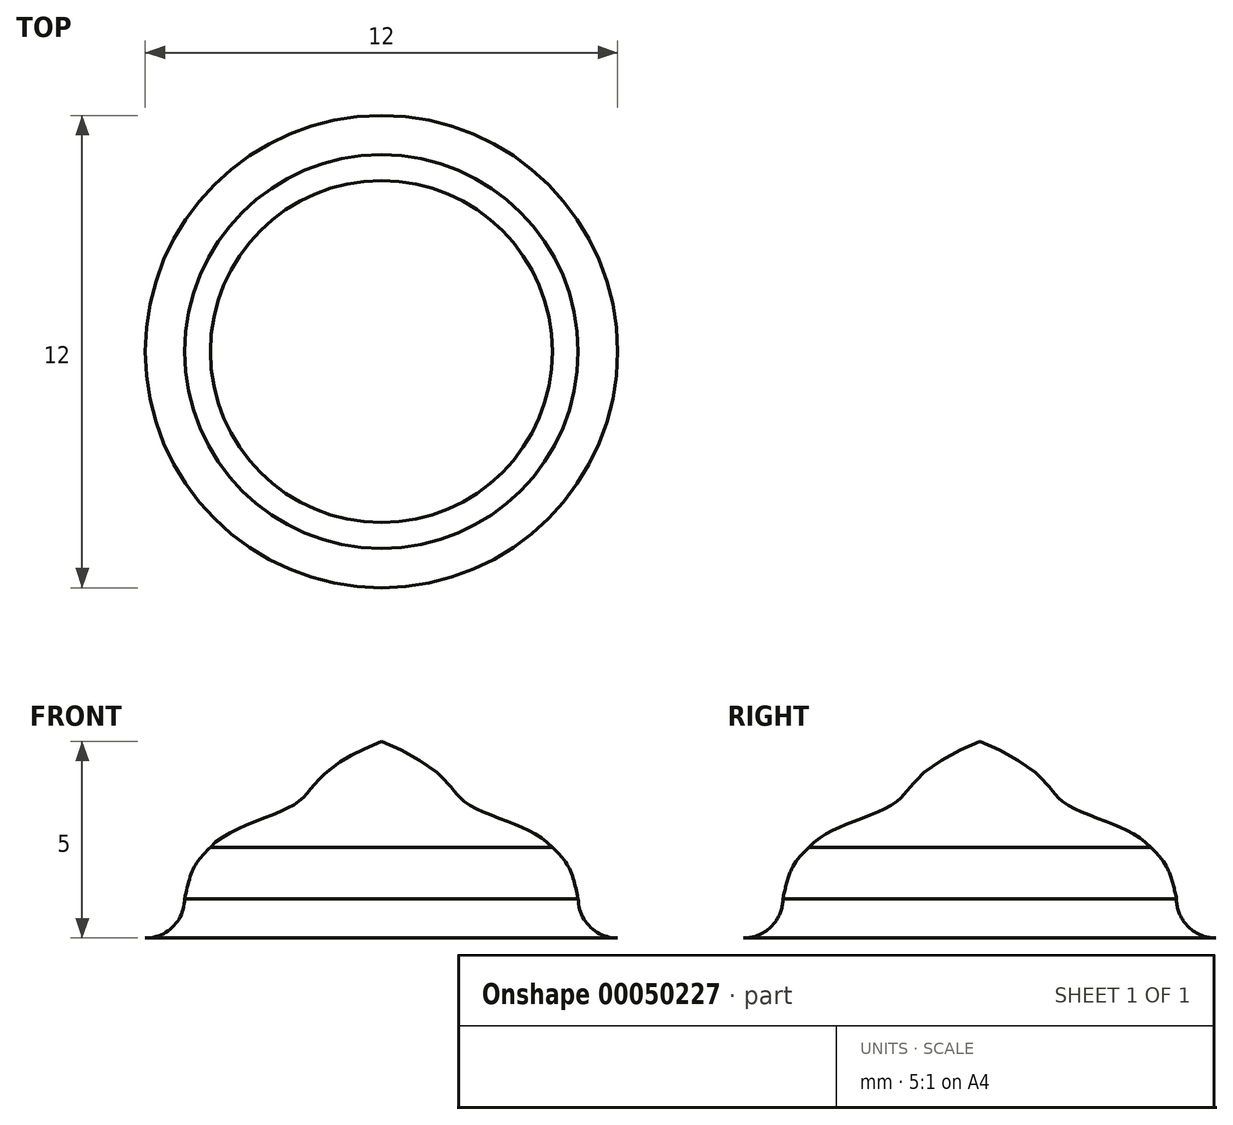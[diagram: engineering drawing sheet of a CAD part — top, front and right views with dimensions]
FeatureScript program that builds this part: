
annotation { "Feature Type Name" : "Feature", "Feature Type Description" : "" }
export const myFeature = defineFeature(function(context is Context, id is Id, definition is map)
    precondition{}
    {
        {
            var Q0;
            Q0=qCreatedBy(makeId("Front.planeOp"),FACE);
            var sketch = newSketch(context, id + "F0", { "sketchPlane" : qUnion([Q0])});
            skLineSegment(sketch, "E0", {"start": v(0, 0) * mm, "end": v(-5, 0) * mm});
            skLineSegment(sketch, "E1", {"start": v(0, -5) * mm, "end": v(0, 0) * mm});
            skFitSpline(sketch, "E2", {"points": [v(-5, 0) * mm, v(-4.34, -2.3) * mm, v(-2.2, -3.4) * mm, v(0, -5) * mm], "startDerivative": vector(4.28, -8.62) * mm, "endDerivative": vector(15.84, -6.66) * mm});
            skLineSegment(sketch, "E3", {"start": v(-5, 0) * mm, "end": v(-6, 0) * mm});
            skLineSegment(sketch, "E4", {"start": v(-5, 0) * mm, "end": v(-5, -1) * mm, "construction": true});
            skArc(sketch, "E5", {"start": v(-5, -1) * mm, "mid": v(-5.3, -0.3) * mm, "end": v(-6, 0) * mm});
            skFitSpline(sketch, "E6", {"points": [v(-4.34, -2.3) * mm, v(-4.74, -1.84) * mm, v(-5, -1) * mm], "startDerivative": vector(-0.95, 0.9) * mm, "endDerivative": vector(-0.37, 1.67) * mm});
            skSolve(sketch);
        }
        {
            var Q0;
            Q0=qSketchRegion(id+"F0",true);
            var Q1;
            Q1=sQuery(id+"F0.wireOp",EDGE,"E1");
            revolve(context, id + "F1", {"entities" : qUnion([Q0]), "axis" : qUnion([Q1]), "revolveType" : RevolveType.FULL});
        }
        {
            var Q0;
            Q0=makeQuery(id+"F1.opRevolve","SWEPT_BODY",BODY,{"disambiguationData":[OSD([sQuery(id+"F0.wireOp",EDGE,"E0"),sQuery(id+"F0.wireOp",EDGE,"E1"),sQuery(id+"F0.wireOp",EDGE,"E2")])]});
            var Q1;
            Q1=sQuery(id+"F0.wireOp",EDGE,"E0");
            transform(context, id + "F2", {"entities" : qUnion([Q0]), "transformType" : TransformType.ROTATION, "transformAxis" : qUnion([Q1]), "angle" : 180 * degree, "makeCopy" : false});
        }
    });
